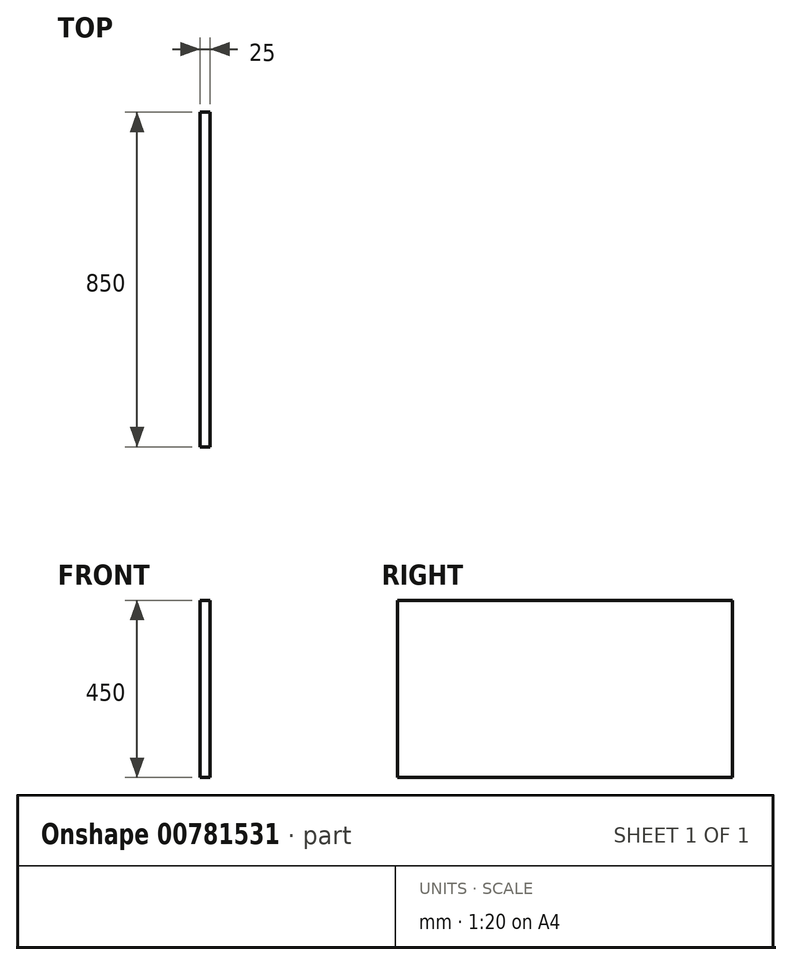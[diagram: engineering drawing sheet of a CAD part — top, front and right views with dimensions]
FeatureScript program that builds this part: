
annotation { "Feature Type Name" : "Feature", "Feature Type Description" : "" }
export const myFeature = defineFeature(function(context is Context, id is Id, definition is map)
    precondition{}
    {
        {
            var Q0;
            Q0=qCreatedBy(makeId("Right.planeOp"),FACE);
            var sketch = newSketch(context, id + "F0", { "sketchPlane" : qUnion([Q0])});
            skLineSegment(sketch, "E0.bottom", {"start": v(0, 0) * mm, "end": v(850, 0) * mm});
            skLineSegment(sketch, "E0.top", {"start": v(0, 450) * mm, "end": v(850, 450) * mm});
            skLineSegment(sketch, "E0.left", {"start": v(0, 0) * mm, "end": v(0, 450) * mm});
            skLineSegment(sketch, "E0.right", {"start": v(850, 0) * mm, "end": v(850, 450) * mm});
            skSolve(sketch);
        }
        {
            var Q0;
            Q0=qSketchRegion(id+"F0",true);
            extrude(context, id + "F1", {"entities" : qUnion([Q0]), "depth" : 25 * mm, "offsetDistance" : 25 * mm});
        }
    });
